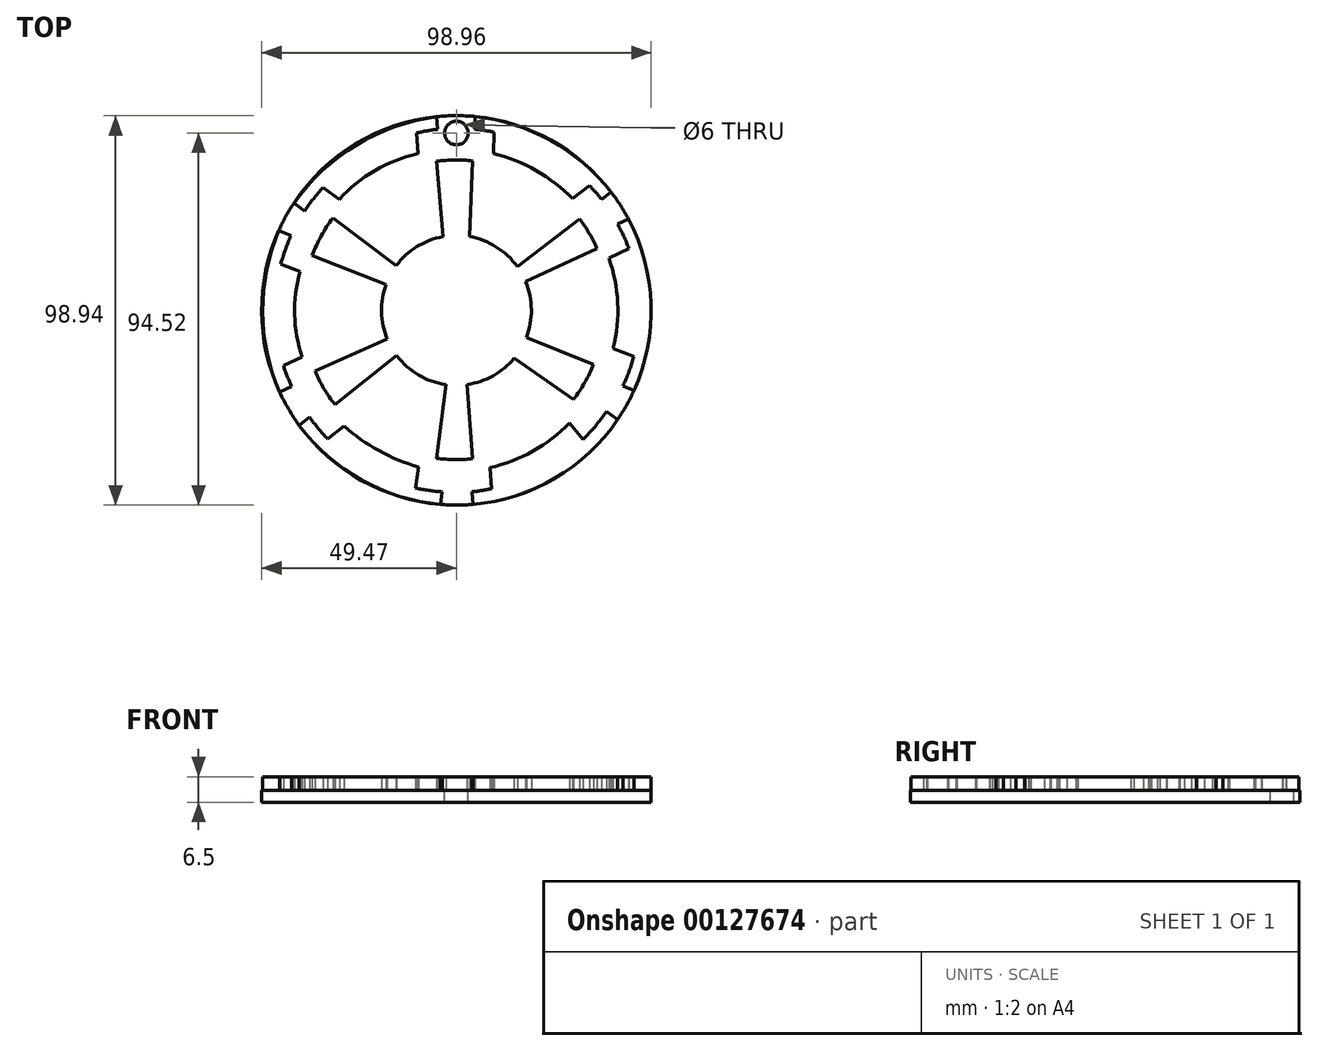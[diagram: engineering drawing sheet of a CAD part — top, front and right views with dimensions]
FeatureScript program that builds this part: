
annotation { "Feature Type Name" : "Feature", "Feature Type Description" : "" }
export const myFeature = defineFeature(function(context is Context, id is Id, definition is map)
    precondition{}
    {
        {
            var Q0;
            Q0=qCreatedBy(makeId("Top.planeOp"),FACE);
            var sketch = newSketch(context, id + "F0", { "sketchPlane" : qUnion([Q0])});
            skCircle(sketch, "E0", {"center": v(0, 0) * mm, "radius": 49.47 * mm});
            skSolve(sketch);
        }
        {
            var Q0;
            Q0 = qSketchRegion(id + "F0", true);
            extrude(context, id + "F1", {"entities" : qUnion([Q0]), "depth" : 3 * mm});
        }
        {
            var Q0;
            Q0=makeQuery(id+"F1.opExtrude","CAP_FACE",FACE,{"disambiguationData":[OSD([sQuery(id+"F0.wireOp",EDGE,"E0")])],"isStart":false});
            var sketch = newSketch(context, id + "F2", { "sketchPlane" : qUnion([Q0])});
            skCircle(sketch, "E1", {"center": v(0, 0) * mm, "radius": 19.04 * mm});
            skLineSegment(sketch, "E2", {"start": v(-3.44, 18.73) * mm, "end": v(-4.99, 37.88) * mm});
            skLineSegment(sketch, "E3", {"start": v(3.28, 18.76) * mm, "end": v(4.1, 37.98) * mm});
            skArc(sketch, "E4", {"start": v(4.1, 37.98) * mm, "mid": v(-0.44, 38.2) * mm, "end": v(-4.99, 37.88) * mm});
            skLineSegment(sketch, "E5", {"start": v(-2.66, -18.85) * mm, "end": v(-4.99, -37.58) * mm});
            skLineSegment(sketch, "E6", {"start": v(2.69, -18.85) * mm, "end": v(4.1, -37.69) * mm});
            skArc(sketch, "E7", {"start": v(-4.99, -37.58) * mm, "mid": v(-0.44, -37.9) * mm, "end": v(4.1, -37.69) * mm});
            skPoint(sketch, "E8", {"position": v(-36.62, 13.96) * mm});
            skPoint(sketch, "E9", {"position": v(-31.39, 23.47) * mm});
            skPoint(sketch, "E10", {"position": v(34.8, -13.72) * mm});
            skPoint(sketch, "E11", {"position": v(29.8, -22.62) * mm});
            skPoint(sketch, "E12", {"position": v(-17.87, 6.57) * mm});
            skPoint(sketch, "E13", {"position": v(-15.3, 11.33) * mm});
            skPoint(sketch, "E14", {"position": v(17.76, -6.86) * mm});
            skPoint(sketch, "E15", {"position": v(14.65, -12.16) * mm});
            skLineSegment(sketch, "E16", {"start": v(-36.62, 13.96) * mm, "end": v(-17.87, 6.57) * mm});
            skLineSegment(sketch, "E17", {"start": v(-31.39, 23.47) * mm, "end": v(-15.3, 11.33) * mm});
            skLineSegment(sketch, "E18", {"start": v(17.76, -6.86) * mm, "end": v(34.8, -13.72) * mm});
            skLineSegment(sketch, "E19", {"start": v(14.65, -12.16) * mm, "end": v(29.8, -22.62) * mm});
            skArc(sketch, "E20", {"start": v(-31.39, 23.47) * mm, "mid": v(-34.34, 18.9) * mm, "end": v(-36.62, 13.96) * mm});
            skArc(sketch, "E21", {"start": v(29.8, -22.62) * mm, "mid": v(32.6, -18.35) * mm, "end": v(34.8, -13.72) * mm});
            skPoint(sketch, "E22", {"position": v(31.33, 23.25) * mm});
            skPoint(sketch, "E23", {"position": v(35.74, 15.64) * mm});
            skPoint(sketch, "E24", {"position": v(-30.89, -23.97) * mm});
            skPoint(sketch, "E25", {"position": v(-35.95, -15.38) * mm});
            skPoint(sketch, "E26", {"position": v(-15.18, -11.5) * mm});
            skPoint(sketch, "E27", {"position": v(-17.57, -7.33) * mm});
            skPoint(sketch, "E28", {"position": v(15.47, 11.1) * mm});
            skPoint(sketch, "E29", {"position": v(17.58, 7.3) * mm});
            skLineSegment(sketch, "E30", {"start": v(-30.89, -23.97) * mm, "end": v(-15.18, -11.5) * mm});
            skLineSegment(sketch, "E31", {"start": v(-17.57, -7.33) * mm, "end": v(-35.95, -15.38) * mm});
            skLineSegment(sketch, "E32", {"start": v(17.58, 7.3) * mm, "end": v(35.74, 15.64) * mm});
            skLineSegment(sketch, "E33", {"start": v(15.47, 11.1) * mm, "end": v(31.33, 23.25) * mm});
            skArc(sketch, "E34", {"start": v(-35.95, -15.38) * mm, "mid": v(-33.7, -19.84) * mm, "end": v(-30.89, -23.97) * mm});
            skArc(sketch, "E35", {"start": v(35.74, 15.64) * mm, "mid": v(33.75, 19.57) * mm, "end": v(31.33, 23.25) * mm});
            skArc(sketch, "E36", {"start": v(-5.02, 49.22) * mm, "mid": v(-25.42, 42) * mm, "end": v(-41.28, 27.27) * mm});
            skArc(sketch, "E37", {"start": v(39.33, 30.01) * mm, "mid": v(24, 43.12) * mm, "end": v(4.78, 49.24) * mm});
            skArc(sketch, "E38", {"start": v(45.1, -20.34) * mm, "mid": v(49.47, 1.6) * mm, "end": v(43.7, 23.2) * mm});
            skArc(sketch, "E39", {"start": v(4.22, -49.3) * mm, "mid": v(25.03, -42.65) * mm, "end": v(40.98, -27.72) * mm});
            skArc(sketch, "E40", {"start": v(-39.93, -29.2) * mm, "mid": v(-24.13, -43.08) * mm, "end": v(-4.04, -49.3) * mm});
            skArc(sketch, "E41", {"start": v(-45.14, 20.25) * mm, "mid": v(-49.21, -0.27) * mm, "end": v(-44.91, -20.74) * mm});
            skLineSegment(sketch, "E42", {"start": v(-44.91, -20.74) * mm, "end": v(-41.82, -19.39) * mm});
            skLineSegment(sketch, "E43", {"start": v(-45.14, 20.25) * mm, "end": v(-42, 19) * mm});
            skLineSegment(sketch, "E44", {"start": v(-41.28, 27.27) * mm, "end": v(-38.59, 25.24) * mm});
            skLineSegment(sketch, "E45", {"start": v(-5.02, 49.22) * mm, "end": v(-4.76, 46.01) * mm});
            skLineSegment(sketch, "E46", {"start": v(4.78, 49.24) * mm, "end": v(4.64, 46.07) * mm});
            skLineSegment(sketch, "E47", {"start": v(39.33, 30.01) * mm, "end": v(36.91, 28.16) * mm});
            skLineSegment(sketch, "E48", {"start": v(43.7, 23.2) * mm, "end": v(40.94, 21.93) * mm});
            skLineSegment(sketch, "E49", {"start": v(45.1, -20.34) * mm, "end": v(42.29, -19.2) * mm});
            skLineSegment(sketch, "E50", {"start": v(40.98, -27.72) * mm, "end": v(38.1, -25.73) * mm});
            skLineSegment(sketch, "E51", {"start": v(4.22, -49.3) * mm, "end": v(3.98, -46.1) * mm});
            skLineSegment(sketch, "E52", {"start": v(-4.04, -49.3) * mm, "end": v(-3.64, -46.1) * mm});
            skLineSegment(sketch, "E53", {"start": v(-39.93, -29.2) * mm, "end": v(-37.3, -27.11) * mm});
            skArc(sketch, "E54", {"start": v(-42, 19) * mm, "mid": v(-46.17, -0.2) * mm, "end": v(-41.82, -19.39) * mm});
            skArc(sketch, "E55", {"start": v(-4.76, 46.01) * mm, "mid": v(-23.96, 39.34) * mm, "end": v(-38.59, 25.24) * mm});
            skArc(sketch, "E56", {"start": v(36.91, 28.16) * mm, "mid": v(22.56, 40.33) * mm, "end": v(4.64, 46.07) * mm});
            skArc(sketch, "E57", {"start": v(42.29, -19.2) * mm, "mid": v(46.64, 1.53) * mm, "end": v(40.94, 21.93) * mm});
            skArc(sketch, "E58", {"start": v(3.98, -46.1) * mm, "mid": v(23.28, -39.67) * mm, "end": v(38.1, -25.73) * mm});
            skArc(sketch, "E59", {"start": v(-37.3, -27.11) * mm, "mid": v(-22.63, -40.44) * mm, "end": v(-3.64, -46.1) * mm});
            skLineSegment(sketch, "E60", {"start": v(-44.61, 11.77) * mm, "end": v(-39.76, 9.82) * mm});
            skLineSegment(sketch, "E61", {"start": v(-43.95, -14) * mm, "end": v(-39.18, -11.91) * mm});
            skLineSegment(sketch, "E62", {"start": v(-32.72, -32.66) * mm, "end": v(-28.55, -29.34) * mm});
            skLineSegment(sketch, "E63", {"start": v(-10.34, -45.15) * mm, "end": v(-9.67, -39.8) * mm});
            skLineSegment(sketch, "E64", {"start": v(8.9, -45.32) * mm, "end": v(8.5, -39.97) * mm});
            skLineSegment(sketch, "E65", {"start": v(28.75, -28.62) * mm, "end": v(32.11, -32.86) * mm});
            skLineSegment(sketch, "E66", {"start": v(-33.85, 31.25) * mm, "end": v(-29.74, 28.15) * mm});
            skLineSegment(sketch, "E67", {"start": v(-10.17, 45.05) * mm, "end": v(-9.75, 39.79) * mm});
            skLineSegment(sketch, "E68", {"start": v(9.62, 45.23) * mm, "end": v(9.39, 39.86) * mm});
            skLineSegment(sketch, "E69", {"start": v(33.83, 31.67) * mm, "end": v(29.53, 28.38) * mm});
            skLineSegment(sketch, "E70", {"start": v(38.72, 13.33) * mm, "end": v(43.84, 15.68) * mm});
            skLineSegment(sketch, "E71", {"start": v(39.8, -9.65) * mm, "end": v(45.06, -11.77) * mm});
            skArc(sketch, "E72", {"start": v(-39.76, 9.82) * mm, "mid": v(-41.1, -1.1) * mm, "end": v(-39.18, -11.91) * mm});
            skArc(sketch, "E73", {"start": v(-9.75, 39.79) * mm, "mid": v(-20.67, 35.56) * mm, "end": v(-29.74, 28.15) * mm});
            skArc(sketch, "E74", {"start": v(29.53, 28.38) * mm, "mid": v(20.25, 35.51) * mm, "end": v(9.39, 39.86) * mm});
            skArc(sketch, "E75", {"start": v(39.8, -9.65) * mm, "mid": v(40.97, 1.92) * mm, "end": v(38.72, 13.33) * mm});
            skArc(sketch, "E76", {"start": v(8.5, -39.97) * mm, "mid": v(19.44, -35.75) * mm, "end": v(28.75, -28.62) * mm});
            skArc(sketch, "E77", {"start": v(-28.55, -29.34) * mm, "mid": v(-19.7, -35.65) * mm, "end": v(-9.67, -39.8) * mm});
            skSolve(sketch);
        }
        {
            var Q0;
            Q0 = qSketchRegion(id + "F2", true);
            extrude(context, id + "F3", {"entities" : qUnion([Q0]), "operationType" : NewBodyOperationType.ADD, "depth" : 3.5 * mm});
        }
        {
            var Q0;
            {var subQ0=sQuery(id+"F2.wireOp",EDGE,"E54");var subQ1=sQuery(id+"F2.wireOp",EDGE,"E43");var subQ2=sQuery(id+"F2.wireOp",EDGE,"E60");var subQ3=sQuery(id+"F2.wireOp",EDGE,"E50");var subQ4=sQuery(id+"F2.wireOp",EDGE,"E53");var subQ5=sQuery(id+"F2.wireOp",EDGE,"E49");var subQ6=sQuery(id+"F2.wireOp",EDGE,"E52");var subQ7=sQuery(id+"F2.wireOp",EDGE,"E48");var subQ8=sQuery(id+"F2.wireOp",EDGE,"E46");var subQ9=sQuery(id+"F2.wireOp",EDGE,"E32");var subQ10=sQuery(id+"F2.wireOp",EDGE,"E64");var subQ11=sQuery(id+"F2.wireOp",EDGE,"E45");var subQ12=sQuery(id+"F2.wireOp",EDGE,"E44");var subQ13=sQuery(id+"F2.wireOp",EDGE,"E42");var subQ14=sQuery(id+"F2.wireOp",EDGE,"E62");var subQ15=sQuery(id+"F2.wireOp",EDGE,"E6");var subQ16=sQuery(id+"F2.wireOp",EDGE,"E38");var subQ17=sQuery(id+"F2.wireOp",EDGE,"E33");var subQ18=sQuery(id+"F2.wireOp",EDGE,"E1");var subQ19=sQuery(id+"F2.wireOp",EDGE,"E19");var subQ20=sQuery(id+"F2.wireOp",EDGE,"E51");var subQ21=sQuery(id+"F2.wireOp",EDGE,"E47");var subQ22=sQuery(id+"F2.wireOp",EDGE,"E17");var subQ23=sQuery(id+"F2.wireOp",EDGE,"E3");var subQ24=sQuery(id+"F2.wireOp",EDGE,"E16");var subQ25=sQuery(id+"F2.wireOp",EDGE,"E31");var subQ26=sQuery(id+"F2.wireOp",EDGE,"E63");var subQ27=sQuery(id+"F2.wireOp",EDGE,"E5");var subQ28=sQuery(id+"F2.wireOp",EDGE,"E30");var subQ29=sQuery(id+"F2.wireOp",EDGE,"E2");var subQ30=sQuery(id+"F0.wireOp",EDGE,"E0");var subQ31=sQuery(id+"F2.wireOp",EDGE,"E56");var subQ32=sQuery(id+"F2.wireOp",EDGE,"E69");var subQ33=makeQuery(id+"F1.opExtrude","CAP_FACE",FACE,{"disambiguationData":[OSD([subQ30])],"isStart":false});var subQ34=sQuery(id+"F2.wireOp",EDGE,"E18");var subQ35=sQuery(id+"F2.wireOp",EDGE,"E75");var subQ36=sQuery(id+"F2.wireOp",EDGE,"E71");var subQ37=sQuery(id+"F2.wireOp",EDGE,"E70");var subQ38=sQuery(id+"F2.wireOp",EDGE,"E57");var subQ39=sQuery(id+"F2.wireOp",EDGE,"E61");var subQ40=sQuery(id+"F2.wireOp",EDGE,"E59");var subQ41=sQuery(id+"F2.wireOp",EDGE,"E55");var subQ42=sQuery(id+"F2.wireOp",EDGE,"E67");var subQ43=sQuery(id+"F2.wireOp",EDGE,"E66");var subQ44=sQuery(id+"F2.wireOp",EDGE,"E68");var subQ45=sQuery(id+"F2.wireOp",EDGE,"E58");var subQ46=sQuery(id+"F2.wireOp",EDGE,"E65");Q0=makeQuery(id+"F3.boolean.opBoolean","SPLIT",FACE,{"disambiguationData":[TD([makeQuery(id+"F1.opExtrude","SWEPT_FACE",FACE,{"disambiguationData":[OSD([subQ30])]}),subQ33,makeQuery(id+"F3.opExtrude","SWEPT_FACE",FACE,{"disambiguationData":[OSD([subQ18]),TDD([makeQuery(id+"F2.imprint","IMPRINT",EDGE,{"disambiguationData":[TD([[makeQuery(id+"F2.imprint","INTERSECT",VERTEX,{"derivedFrom":[subQ18,subQ23]}),1.0]])],"derivedFrom":subQ18})])]}),makeQuery(id+"F3.opExtrude","SWEPT_FACE",FACE,{"disambiguationData":[OSD([subQ18]),TDD([makeQuery(id+"F2.imprint","IMPRINT",EDGE,{"disambiguationData":[TD([[makeQuery(id+"F2.imprint","INTERSECT",VERTEX,{"derivedFrom":[subQ18,subQ29]}),-1.0]])],"derivedFrom":subQ18})])]}),makeQuery(id+"F3.opExtrude","SWEPT_FACE",FACE,{"disambiguationData":[OSD([subQ18]),TDD([makeQuery(id+"F2.imprint","IMPRINT",EDGE,{"disambiguationData":[TD([[makeQuery(id+"F2.imprint","INTERSECT",VERTEX,{"derivedFrom":[subQ18,subQ24]}),-1.0]])],"derivedFrom":subQ18})])]}),makeQuery(id+"F3.opExtrude","SWEPT_FACE",FACE,{"disambiguationData":[OSD([subQ18]),TDD([makeQuery(id+"F2.imprint","IMPRINT",EDGE,{"disambiguationData":[TD([[makeQuery(id+"F2.imprint","INTERSECT",VERTEX,{"derivedFrom":[subQ18,subQ27]}),1.0]])],"derivedFrom":subQ18})])]}),makeQuery(id+"F3.opExtrude","SWEPT_FACE",FACE,{"disambiguationData":[OSD([subQ18]),TDD([makeQuery(id+"F2.imprint","IMPRINT",EDGE,{"disambiguationData":[TD([[makeQuery(id+"F2.imprint","INTERSECT",VERTEX,{"derivedFrom":[subQ18,subQ15]}),-1.0]])],"derivedFrom":subQ18})])]}),makeQuery(id+"F3.opExtrude","SWEPT_FACE",FACE,{"disambiguationData":[OSD([subQ18]),TDD([makeQuery(id+"F2.imprint","IMPRINT",EDGE,{"disambiguationData":[TD([[makeQuery(id+"F2.imprint","INTERSECT",VERTEX,{"derivedFrom":[subQ18,subQ34]}),-1.0]])],"derivedFrom":subQ18})])]}),makeQuery(id+"F3.opExtrude","SWEPT_FACE",FACE,{"disambiguationData":[OSD([subQ29])]}),makeQuery(id+"F3.opExtrude","SWEPT_FACE",FACE,{"disambiguationData":[OSD([subQ23])]}),makeQuery(id+"F3.opExtrude","SWEPT_FACE",FACE,{"disambiguationData":[OSD([sQuery(id+"F2.wireOp",EDGE,"E4")])]}),makeQuery(id+"F3.opExtrude","SWEPT_FACE",FACE,{"disambiguationData":[OSD([subQ27])]}),makeQuery(id+"F3.opExtrude","SWEPT_FACE",FACE,{"disambiguationData":[OSD([subQ15])]}),makeQuery(id+"F3.opExtrude","SWEPT_FACE",FACE,{"disambiguationData":[OSD([sQuery(id+"F2.wireOp",EDGE,"E7")])]}),makeQuery(id+"F3.opExtrude","SWEPT_FACE",FACE,{"disambiguationData":[OSD([subQ24])]}),makeQuery(id+"F3.opExtrude","SWEPT_FACE",FACE,{"disambiguationData":[OSD([subQ22])]}),makeQuery(id+"F3.opExtrude","SWEPT_FACE",FACE,{"disambiguationData":[OSD([subQ34])]}),makeQuery(id+"F3.opExtrude","SWEPT_FACE",FACE,{"disambiguationData":[OSD([subQ19])]}),makeQuery(id+"F3.opExtrude","SWEPT_FACE",FACE,{"disambiguationData":[OSD([sQuery(id+"F2.wireOp",EDGE,"E20")])]}),makeQuery(id+"F3.opExtrude","SWEPT_FACE",FACE,{"disambiguationData":[OSD([sQuery(id+"F2.wireOp",EDGE,"E21")])]}),makeQuery(id+"F3.opExtrude","SWEPT_FACE",FACE,{"disambiguationData":[OSD([subQ28])]}),makeQuery(id+"F3.opExtrude","SWEPT_FACE",FACE,{"disambiguationData":[OSD([subQ25])]}),makeQuery(id+"F3.opExtrude","SWEPT_FACE",FACE,{"disambiguationData":[OSD([subQ9])]}),makeQuery(id+"F3.opExtrude","SWEPT_FACE",FACE,{"disambiguationData":[OSD([subQ17])]}),makeQuery(id+"F3.opExtrude","SWEPT_FACE",FACE,{"disambiguationData":[OSD([sQuery(id+"F2.wireOp",EDGE,"E34")])]}),makeQuery(id+"F3.opExtrude","SWEPT_FACE",FACE,{"disambiguationData":[OSD([sQuery(id+"F2.wireOp",EDGE,"E35")])]}),makeQuery(id+"F3.opExtrude","SWEPT_FACE",FACE,{"disambiguationData":[OSD([sQuery(id+"F2.wireOp",EDGE,"E36")])]}),makeQuery(id+"F3.opExtrude","SWEPT_FACE",FACE,{"disambiguationData":[OSD([sQuery(id+"F2.wireOp",EDGE,"E37")])]}),makeQuery(id+"F3.opExtrude","SWEPT_FACE",FACE,{"disambiguationData":[OSD([subQ16])]}),makeQuery(id+"F3.opExtrude","CAP_FACE",FACE,{"disambiguationData":[OSD([subQ16,subQ7,subQ5,subQ38,subQ37,subQ36,subQ35])],"isStart":true}),makeQuery(id+"F3.opExtrude","SWEPT_FACE",FACE,{"disambiguationData":[OSD([sQuery(id+"F2.wireOp",EDGE,"E39")])]}),makeQuery(id+"F3.opExtrude","SWEPT_FACE",FACE,{"disambiguationData":[OSD([sQuery(id+"F2.wireOp",EDGE,"E40")])]}),makeQuery(id+"F3.opExtrude","SWEPT_FACE",FACE,{"disambiguationData":[OSD([sQuery(id+"F2.wireOp",EDGE,"E41")])]}),makeQuery(id+"F3.opExtrude","SWEPT_FACE",FACE,{"disambiguationData":[OSD([subQ13])]}),makeQuery(id+"F3.opExtrude","SWEPT_FACE",FACE,{"disambiguationData":[OSD([subQ1])]}),makeQuery(id+"F3.opExtrude","SWEPT_FACE",FACE,{"disambiguationData":[OSD([subQ12])]}),makeQuery(id+"F3.opExtrude","SWEPT_FACE",FACE,{"disambiguationData":[OSD([subQ11])]}),makeQuery(id+"F3.opExtrude","SWEPT_FACE",FACE,{"disambiguationData":[OSD([subQ8])]}),makeQuery(id+"F3.opExtrude","SWEPT_FACE",FACE,{"disambiguationData":[OSD([subQ21])]}),makeQuery(id+"F3.opExtrude","SWEPT_FACE",FACE,{"disambiguationData":[OSD([subQ7])]}),makeQuery(id+"F3.opExtrude","SWEPT_FACE",FACE,{"disambiguationData":[OSD([subQ5])]}),makeQuery(id+"F3.opExtrude","SWEPT_FACE",FACE,{"disambiguationData":[OSD([subQ3])]}),makeQuery(id+"F3.opExtrude","SWEPT_FACE",FACE,{"disambiguationData":[OSD([subQ20])]}),makeQuery(id+"F3.opExtrude","SWEPT_FACE",FACE,{"disambiguationData":[OSD([subQ6])]}),makeQuery(id+"F3.opExtrude","SWEPT_FACE",FACE,{"disambiguationData":[OSD([subQ4])]}),makeQuery(id+"F3.opExtrude","SWEPT_FACE",FACE,{"disambiguationData":[OSD([subQ0]),TDD([makeQuery(id+"F2.imprint","IMPRINT",EDGE,{"disambiguationData":[TD([[makeQuery(id+"F2.imprint","INTERSECT",VERTEX,{"derivedFrom":[subQ1,subQ0]}),-1.0]])],"derivedFrom":subQ0})])]}),makeQuery(id+"F3.opExtrude","SWEPT_FACE",FACE,{"disambiguationData":[OSD([subQ0]),TDD([makeQuery(id+"F2.imprint","IMPRINT",EDGE,{"disambiguationData":[TD([[makeQuery(id+"F2.imprint","INTERSECT",VERTEX,{"derivedFrom":[subQ13,subQ0]}),1.0]])],"derivedFrom":subQ0})])]}),makeQuery(id+"F3.opExtrude","SWEPT_FACE",FACE,{"disambiguationData":[OSD([subQ41]),TDD([makeQuery(id+"F2.imprint","IMPRINT",EDGE,{"disambiguationData":[TD([[makeQuery(id+"F2.imprint","INTERSECT",VERTEX,{"derivedFrom":[subQ11,subQ41]}),-1.0]])],"derivedFrom":subQ41})])]}),makeQuery(id+"F3.opExtrude","SWEPT_FACE",FACE,{"disambiguationData":[OSD([subQ41]),TDD([makeQuery(id+"F2.imprint","IMPRINT",EDGE,{"disambiguationData":[TD([[makeQuery(id+"F2.imprint","INTERSECT",VERTEX,{"derivedFrom":[subQ12,subQ41]}),1.0]])],"derivedFrom":subQ41})])]}),makeQuery(id+"F3.opExtrude","SWEPT_FACE",FACE,{"disambiguationData":[OSD([subQ31]),TDD([makeQuery(id+"F2.imprint","IMPRINT",EDGE,{"disambiguationData":[TD([[makeQuery(id+"F2.imprint","INTERSECT",VERTEX,{"derivedFrom":[subQ21,subQ31]}),-1.0]])],"derivedFrom":subQ31})])]}),makeQuery(id+"F3.opExtrude","SWEPT_FACE",FACE,{"disambiguationData":[OSD([subQ31]),TDD([makeQuery(id+"F2.imprint","IMPRINT",EDGE,{"disambiguationData":[TD([[makeQuery(id+"F2.imprint","INTERSECT",VERTEX,{"derivedFrom":[subQ8,subQ31]}),1.0]])],"derivedFrom":subQ31})])]}),makeQuery(id+"F3.opExtrude","SWEPT_FACE",FACE,{"disambiguationData":[OSD([subQ38]),TDD([makeQuery(id+"F2.imprint","IMPRINT",EDGE,{"disambiguationData":[TD([[makeQuery(id+"F2.imprint","INTERSECT",VERTEX,{"derivedFrom":[subQ5,subQ38]}),-1.0]])],"derivedFrom":subQ38})])]}),makeQuery(id+"F3.opExtrude","SWEPT_FACE",FACE,{"disambiguationData":[OSD([subQ38]),TDD([makeQuery(id+"F2.imprint","IMPRINT",EDGE,{"disambiguationData":[TD([[makeQuery(id+"F2.imprint","INTERSECT",VERTEX,{"derivedFrom":[subQ7,subQ38]}),1.0]])],"derivedFrom":subQ38})])]}),makeQuery(id+"F3.opExtrude","SWEPT_FACE",FACE,{"disambiguationData":[OSD([subQ45]),TDD([makeQuery(id+"F2.imprint","IMPRINT",EDGE,{"disambiguationData":[TD([[makeQuery(id+"F2.imprint","INTERSECT",VERTEX,{"derivedFrom":[subQ20,subQ45]}),-1.0]])],"derivedFrom":subQ45})])]}),makeQuery(id+"F3.opExtrude","SWEPT_FACE",FACE,{"disambiguationData":[OSD([subQ45]),TDD([makeQuery(id+"F2.imprint","IMPRINT",EDGE,{"disambiguationData":[TD([[makeQuery(id+"F2.imprint","INTERSECT",VERTEX,{"derivedFrom":[subQ3,subQ45]}),1.0]])],"derivedFrom":subQ45})])]}),makeQuery(id+"F3.opExtrude","SWEPT_FACE",FACE,{"disambiguationData":[OSD([subQ40]),TDD([makeQuery(id+"F2.imprint","IMPRINT",EDGE,{"disambiguationData":[TD([[makeQuery(id+"F2.imprint","INTERSECT",VERTEX,{"derivedFrom":[subQ4,subQ40]}),-1.0]])],"derivedFrom":subQ40})])]}),makeQuery(id+"F3.opExtrude","SWEPT_FACE",FACE,{"disambiguationData":[OSD([subQ40]),TDD([makeQuery(id+"F2.imprint","IMPRINT",EDGE,{"disambiguationData":[TD([[makeQuery(id+"F2.imprint","INTERSECT",VERTEX,{"derivedFrom":[subQ6,subQ40]}),1.0]])],"derivedFrom":subQ40})])]}),makeQuery(id+"F3.opExtrude","SWEPT_FACE",FACE,{"disambiguationData":[OSD([subQ2])]}),makeQuery(id+"F3.opExtrude","SWEPT_FACE",FACE,{"disambiguationData":[OSD([subQ39])]}),makeQuery(id+"F3.opExtrude","SWEPT_FACE",FACE,{"disambiguationData":[OSD([subQ14])]}),makeQuery(id+"F3.opExtrude","SWEPT_FACE",FACE,{"disambiguationData":[OSD([subQ26])]}),makeQuery(id+"F3.opExtrude","SWEPT_FACE",FACE,{"disambiguationData":[OSD([subQ10])]}),makeQuery(id+"F3.opExtrude","SWEPT_FACE",FACE,{"disambiguationData":[OSD([subQ46])]}),makeQuery(id+"F3.opExtrude","SWEPT_FACE",FACE,{"disambiguationData":[OSD([subQ43])]}),makeQuery(id+"F3.opExtrude","SWEPT_FACE",FACE,{"disambiguationData":[OSD([subQ42])]}),makeQuery(id+"F3.opExtrude","SWEPT_FACE",FACE,{"disambiguationData":[OSD([subQ44])]}),makeQuery(id+"F3.opExtrude","SWEPT_FACE",FACE,{"disambiguationData":[OSD([subQ32])]}),makeQuery(id+"F3.opExtrude","SWEPT_FACE",FACE,{"disambiguationData":[OSD([subQ37])]}),makeQuery(id+"F3.opExtrude","SWEPT_FACE",FACE,{"disambiguationData":[OSD([subQ36])]}),makeQuery(id+"F3.opExtrude","SWEPT_FACE",FACE,{"disambiguationData":[OSD([sQuery(id+"F2.wireOp",EDGE,"E72")])]}),makeQuery(id+"F3.opExtrude","SWEPT_FACE",FACE,{"disambiguationData":[OSD([sQuery(id+"F2.wireOp",EDGE,"E73")])]}),makeQuery(id+"F3.opExtrude","SWEPT_FACE",FACE,{"disambiguationData":[OSD([sQuery(id+"F2.wireOp",EDGE,"E74")])]}),makeQuery(id+"F3.opExtrude","SWEPT_FACE",FACE,{"disambiguationData":[OSD([subQ35])]}),makeQuery(id+"F3.opExtrude","SWEPT_FACE",FACE,{"disambiguationData":[OSD([sQuery(id+"F2.wireOp",EDGE,"E76")])]}),makeQuery(id+"F3.opExtrude","SWEPT_FACE",FACE,{"disambiguationData":[OSD([sQuery(id+"F2.wireOp",EDGE,"E77")])]})])],"derivedFrom":subQ33});}
            var sketch = newSketch(context, id + "F4", { "sketchPlane" : qUnion([Q0])});
            skPoint(sketch, "E78", {"position": v(0, 45.05) * mm});
            skSolve(sketch);
        }
        {
            var Q0;
            Q0=sQuery(id+"F4.wireOp",VERTEX,"E78");
            var Q1;
            Q1=makeQuery(id+"F1.opExtrude","SWEPT_BODY",BODY,{"disambiguationData":[OSD([sQuery(id+"F0.wireOp",EDGE,"E0")])]});
            hole(context, id + "F5", {"style" : HoleStyle.SIMPLE, "endStyle" : HoleEndStyle.THROUGH, "holeDiameter" : 6 * mm, "locations" : qUnion([Q0]), "scope" : qUnion([Q1]), "isTappedThrough" : true});
        }
    });
